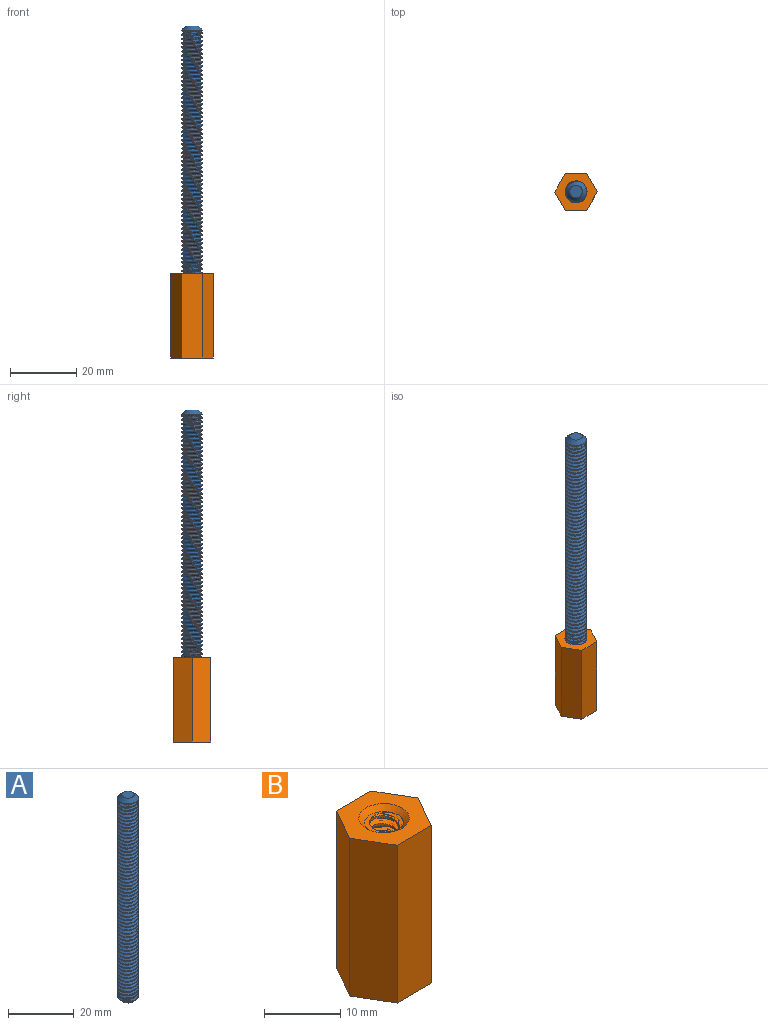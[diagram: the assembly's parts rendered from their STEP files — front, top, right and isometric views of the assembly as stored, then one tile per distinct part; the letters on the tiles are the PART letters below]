
ASSEMBLY  parts=2 mates=1
PART A: 10 faces, bbox 6.7x7.7x76.5 mm
  f0: cylinder r=3.17mm len=73.66mm, axis (0,0,-1), area -116.7mm2, adj f3,f4,f6,f7
  f1: plane 3.81x3.81mm, normal (0,0,1), area 11.4mm2, adj f4
  f2: plane 3.81x3.81mm, normal (0,0,-1), area 11.4mm2, adj f3
  f3: cone r=3.17mm half-angle=45deg, axis (0,0,1), area 28.7mm2, adj f0,f2,f9
  f4: cone r=1.91mm half-angle=45deg, axis (0,0,-1), area 28.7mm2, adj f0,f1,f8
  f5: bspline ~74.61x5.75mm, area 317.9mm2, adj f6,f7,f8,f9
  f6: bspline ~74.69x7.33mm, area 821mm2, adj f0,f5,f8,f9
  f7: bspline ~74.48x7.33mm, area 818.2mm2, adj f0,f5,f8,f9
  f8: plane 6.7x6.7mm, normal (0,0,-1), area 7.2mm2, adj f4,f5,f6,f7
  f9: plane 6.7x6.7mm, normal (0,0,1), area 7.2mm2, adj f3,f5,f6,f7
PART B: 18 faces, bbox 13.1x11.5x25.7 mm
  f0: plane 25.4x6.42mm, normal (0.01,-1,0), area 163mm2, adj f1,f5,f6,f7
  f1: plane 25.4x5.58mm, normal (0.87,-0.49,0), area 163mm2, adj f0,f2,f6,f7
  f2: plane 25.4x5.53mm, normal (0.86,0.51,0), area 163mm2, adj f1,f3,f6,f7
  f3: plane 25.4x6.42mm, normal (-0.01,1,0), area 163mm2, adj f2,f4,f6,f7
  f4: plane 25.4x5.58mm, normal (-0.87,0.49,0), area 163mm2, adj f3,f5,f6,f7
  f5: plane 25.4x5.53mm, normal (-0.86,-0.51,0), area 163mm2, adj f0,f4,f6,f7
  f6: plane 12.83x11.17mm, normal (0,0,1), area 72.4mm2, adj f0,f1,f2,f3,f4,f5,f9
  f7: plane 12.83x11.17mm, normal (0,0,-1), area 72.4mm2, adj f0,f1,f2,f3,f4,f5,f8
  f8: cone r=3.31mm half-angle=45deg, axis (0,0,-1), area 19.9mm2, adj f7,f14,f15
  f9: cone r=2.55mm half-angle=45deg, axis (0,0,1), area 19.9mm2, adj f6,f13,f16
  f10: bspline ~24.74x6.02mm, area 213.3mm2, adj f12,f13,f14,f15,f16,f17
  f11: bspline ~24.95x6.02mm, area 212.7mm2, adj f12,f13,f14,f15,f16,f17
  f12: bspline ~24.29x6.15mm, area 57.4mm2, adj f10,f11,f13,f14
  f13: plane 2.39x1.27mm, normal (0,0,-1), area 0.2mm2, adj f9,f10,f11,f12
  f14: plane 1.93x1.89mm, normal (0,0,1), area 0.2mm2, adj f8,f10,f11,f12
  f15: plane 5.4x5.4mm, normal (0,0,-1), area 4.9mm2, adj f8,f10,f11,f17
  f16: plane 5.41x5.4mm, normal (0,0,1), area 4.9mm2, adj f9,f10,f11,f17
  f17: cylinder r=1.92mm len=23.88mm, axis (0,0,1), area 22mm2, adj f10,f11,f15,f16
PLACE A t=(0,0,25.4)mm fixed
PLACE B t=(0,0,1.59)mm
MATE cylindrical B.f8 <-> A.f0  axis (0,0,1) through (0,0,26.99)mm
